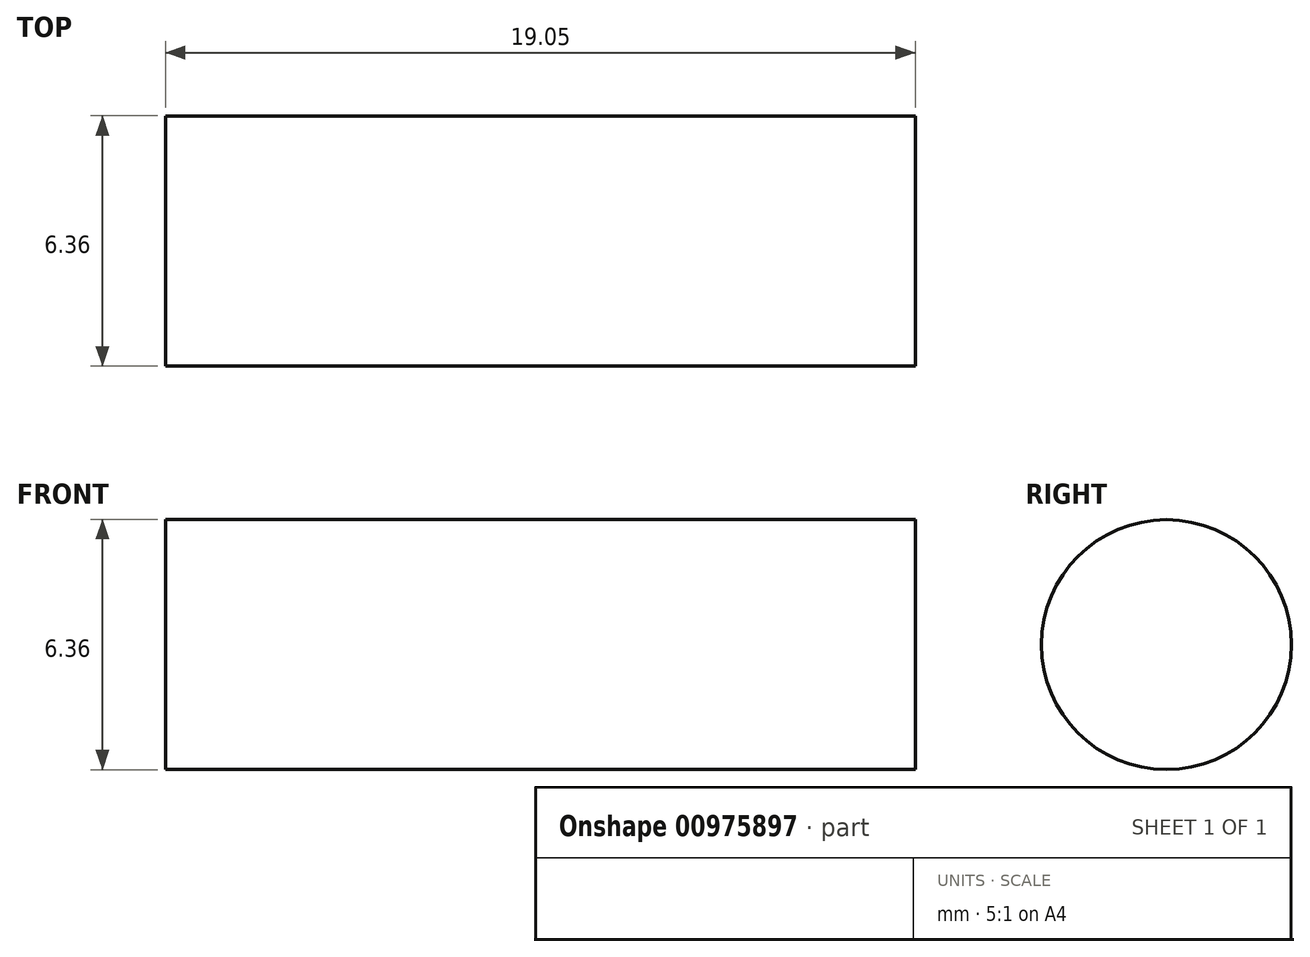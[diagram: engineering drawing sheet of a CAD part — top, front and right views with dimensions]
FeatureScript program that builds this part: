
annotation { "Feature Type Name" : "Feature", "Feature Type Description" : "" }
export const myFeature = defineFeature(function(context is Context, id is Id, definition is map)
    precondition{}
    {
        {
            var Q0;
            Q0=qCreatedBy(makeId("Right.planeOp"),FACE);
            var sketch = newSketch(context, id + "F0", { "sketchPlane" : qUnion([Q0])});
            skCircle(sketch, "E0", {"center": v(0, 0) * mm, "radius": 3.18 * mm});
            skSolve(sketch);
        }
        {
            var Q0;
            Q0 = qSketchRegion(id + "F0", true);
            extrude(context, id + "F1", {"entities" : qUnion([Q0]), "depth" : 19.05 * mm, "offsetDistance" : 25.4 * mm});
        }
    });
